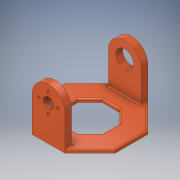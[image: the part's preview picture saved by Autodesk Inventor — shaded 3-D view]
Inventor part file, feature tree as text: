
AUTODESK INVENTOR PART (.ipt)
format: ipt  version: 2017 (Build 210142000, 142)  size: 243,200 bytes
history: native  units: mm
features: extrude x6, sketch x6, fillet x3, chamfer x1
ambient origin geometry x8: Origin, YZ Plane, XZ Plane, XY Plane, X Axis, Y Axis, Z Axis, Center Point
bodies: Solid1 (feature_tree)
feature tree (16):
  extrude  "Extrusion1"  Depth=61.0mm
  extrude  "Extrusion2"  TaperAngle=0.0deg  [1 undecoded]
  chamfer  "Chamfer1"  Distance=18.5mm
  fillet  "Fillet3"  Radius=2.0mm
  fillet  "Fillet4"  Radius=10.0mm
  extrude  "Extrusion3"  Depth=10.0mm
  extrude  "Extrusion4"  Depth=10.0mm
  extrude  "Extrusion5"  Depth=10.0mm
  fillet  "Fillet5"  Radius=7.0mm
  extrude  "Extrusion6"  Depth=10.0mm
  sketch  "Sketch1"  dims[d0=61.0mm d1=61.0mm]
  sketch  "Sketch2"  dims[d2=2.5mm d3=0.0mm]
  sketch  "Sketch3"  dims[d4=5.0mm]
  sketch  "Sketch4"  dims[d5=35.5mm]
  sketch  "Sketch5"  dims[d6=0.0mm]
  sketch  "Sketch6"  dims[d7=24.0mm d8=18.5mm d9=2.0mm d10=45.0deg d11=10.0mm d12=0.0mm d13=2.0mm d14=7.0mm d15=7.0mm d16=7.0mm d17=7.0mm d18=13.0mm d19=10.0mm d20=0.0mm d21=15.0mm d22=10.0mm d23=0.0mm d24=1.0mm d25=7.7mm d26=10.0mm d27=0.0mm]
note: 1 required parameter value undecoded (feature->parameter linkage not recoverable at this tier; creation-order binding heuristic only, values carry confidence <= 0.55)
